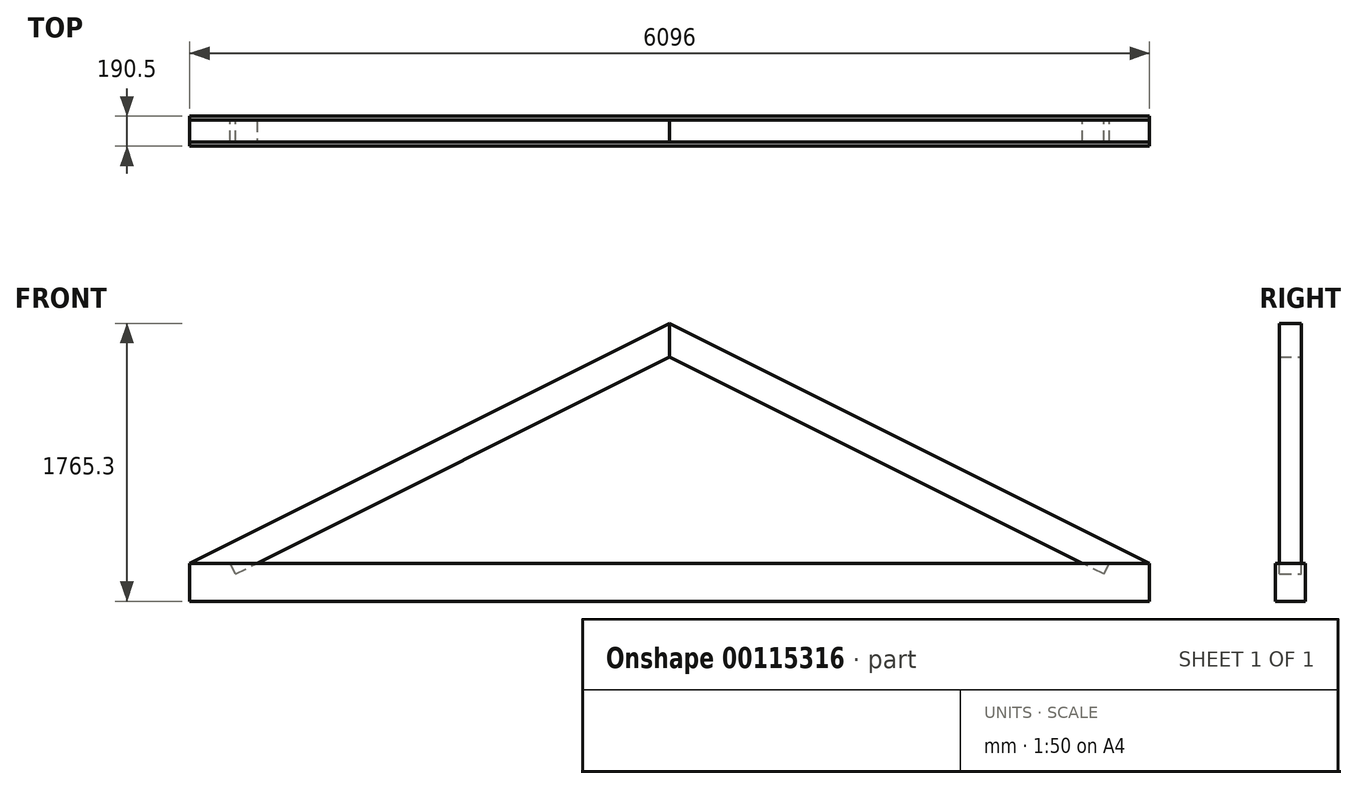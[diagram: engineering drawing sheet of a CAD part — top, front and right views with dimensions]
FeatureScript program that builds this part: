
annotation { "Feature Type Name" : "Feature", "Feature Type Description" : "" }
export const myFeature = defineFeature(function(context is Context, id is Id, definition is map)
    precondition{}
    {
        {
            var Q0;
            Q0=qCreatedBy(makeId("Front.planeOp"),FACE);
            var sketch = newSketch(context, id + "F0", { "sketchPlane" : qUnion([Q0])});
            skLineSegment(sketch, "E0", {"start": v(0, 0) * mm, "end": v(0, 1524) * mm});
            skLineSegment(sketch, "E1", {"start": v(0, 1524) * mm, "end": v(-3048, 0) * mm});
            skLineSegment(sketch, "E2", {"start": v(-3048, 0) * mm, "end": v(-3048, -241.3) * mm});
            skLineSegment(sketch, "E3", {"start": v(-3048, -241.3) * mm, "end": v(0, -241.3) * mm});
            skLineSegment(sketch, "E4", {"start": v(0, -241.3) * mm, "end": v(0, 0) * mm});
            skLineSegment(sketch, "E5", {"start": v(-3048, 0) * mm, "end": v(0, 0) * mm});
            skLineSegment(sketch, "E6", {"start": v(-2622.03, 0) * mm, "end": v(0, 1311.01) * mm});
            skLineSegment(sketch, "E7", {"start": v(0, 1524) * mm, "end": v(-304.8, 1524) * mm});
            skLineSegment(sketch, "E8", {"start": v(-304.8, 1524) * mm, "end": v(-304.8, 1371.6) * mm});
            skLineSegment(sketch, "E9.MirrorCS", {"start": v(0, 1524) * mm, "end": v(3048, 0) * mm});
            skLineSegment(sketch, "E10.MirrorCS", {"start": v(2622.03, 0) * mm, "end": v(0, 1311.01) * mm});
            skLineSegment(sketch, "E11.MirrorCS", {"start": v(3048, 0) * mm, "end": v(0, 0) * mm});
            skLineSegment(sketch, "E12.MirrorCS", {"start": v(3048, 0) * mm, "end": v(3048, -241.3) * mm});
            skLineSegment(sketch, "E13.MirrorCS", {"start": v(3048, -241.3) * mm, "end": v(0, -241.3) * mm});
            skLineSegment(sketch, "E14", {"start": v(-2622.03, 0) * mm, "end": v(-2758.34, -68.16) * mm});
            skLineSegment(sketch, "E15", {"start": v(-2758.34, -68.16) * mm, "end": v(-2792.42, 0) * mm});
            skSolve(sketch);
        }
        {
            var Q0;
            {var subQ1=sQuery(id+"F0.wireOp",EDGE,"E2");Q0=makeQuery(id+"F0.imprint","IMPRINT",FACE,{"disambiguationData":[TD([[makeQuery(id+"F0.imprint","IMPRINT",EDGE,{"derivedFrom":subQ1}),1.0]])]});}
            var Q1;
            {var subQ2=sQuery(id+"F0.wireOp",EDGE,"E4");Q1=makeQuery(id+"F0.imprint","IMPRINT",FACE,{"disambiguationData":[TD([[makeQuery(id+"F0.imprint","IMPRINT",EDGE,{"derivedFrom":subQ2}),-1.0]])]});}
            var Q2;
            {var subQ0=sQuery(id+"F0.wireOp",EDGE,"E14");Q2=makeQuery(id+"F0.imprint","IMPRINT",FACE,{"disambiguationData":[TD([[makeQuery(id+"F0.imprint","IMPRINT",EDGE,{"derivedFrom":subQ0}),-1.0]])]});}
            extrude(context, id + "F1", {"entities" : qUnion([Q0, Q1, Q2]), "endBound" : BoundingType.SYMMETRIC, "depth" : 190.5 * mm});
        }
        {
            var Q0;
            {var subQ3=sQuery(id+"F0.wireOp",EDGE,"E6");Q0=makeQuery(id+"F0.imprint","IMPRINT",FACE,{"disambiguationData":[TD([[makeQuery(id+"F0.imprint","IMPRINT",EDGE,{"derivedFrom":subQ3}),1.0]])]});}
            var Q1;
            {var subQ0=sQuery(id+"F0.wireOp",EDGE,"E14");Q1=makeQuery(id+"F0.imprint","IMPRINT",FACE,{"disambiguationData":[TD([[makeQuery(id+"F0.imprint","IMPRINT",EDGE,{"derivedFrom":subQ0}),-1.0]])]});}
            extrude(context, id + "F2", {"entities" : qUnion([Q0, Q1]), "endBound" : BoundingType.SYMMETRIC, "depth" : 139.7 * mm});
        }
        {
            var Q0;
            Q0=makeQuery(id+"F2.opExtrude","SWEPT_BODY",BODY,{"disambiguationData":[OSD([sQuery(id+"F0.wireOp",EDGE,"E0"),sQuery(id+"F0.wireOp",EDGE,"E1"),sQuery(id+"F0.wireOp",EDGE,"E5"),sQuery(id+"F0.wireOp",EDGE,"E6"),sQuery(id+"F0.wireOp",EDGE,"E14"),sQuery(id+"F0.wireOp",EDGE,"E15")])]});
            var Q1;
            Q1=qCreatedBy(makeId("Right.planeOp"),FACE);
            mirror(context, id + "F3", {"entities" : qUnion([Q0]), "mirrorPlane" : qUnion([Q1])});
        }
        {
            var Q0;
            Q0=makeQuery(id+"F2.opExtrude","SWEPT_BODY",BODY,{"disambiguationData":[OSD([sQuery(id+"F0.wireOp",EDGE,"E0"),sQuery(id+"F0.wireOp",EDGE,"E1"),sQuery(id+"F0.wireOp",EDGE,"E5"),sQuery(id+"F0.wireOp",EDGE,"E6"),sQuery(id+"F0.wireOp",EDGE,"E14"),sQuery(id+"F0.wireOp",EDGE,"E15")])]});
            var Q1;
            Q1=makeQuery(id+"F3.opPattern","COPY",BODY,{"derivedFrom":makeQuery(id+"F2.opExtrude","SWEPT_BODY",BODY,{"disambiguationData":[OSD([sQuery(id+"F0.wireOp",EDGE,"E0"),sQuery(id+"F0.wireOp",EDGE,"E1"),sQuery(id+"F0.wireOp",EDGE,"E5"),sQuery(id+"F0.wireOp",EDGE,"E6"),sQuery(id+"F0.wireOp",EDGE,"E14"),sQuery(id+"F0.wireOp",EDGE,"E15")])]}),"instanceName":"1"});
            var Q2;
            Q2=makeQuery(id+"F1.opExtrude","SWEPT_BODY",BODY,{"disambiguationData":[OSD([sQuery(id+"F0.wireOp",EDGE,"E2"),sQuery(id+"F0.wireOp",EDGE,"E3"),sQuery(id+"F0.wireOp",EDGE,"E5"),sQuery(id+"F0.wireOp",EDGE,"E11.MirrorCS"),sQuery(id+"F0.wireOp",EDGE,"E12.MirrorCS"),sQuery(id+"F0.wireOp",EDGE,"E13.MirrorCS")])]});
            booleanBodies(context, id + "F4", {"operationType" : BooleanOperationType.SUBTRACTION, "tools" : qUnion([Q0, Q1]), "targets" : qUnion([Q2]), "keepTools" : true});
        }
    });
